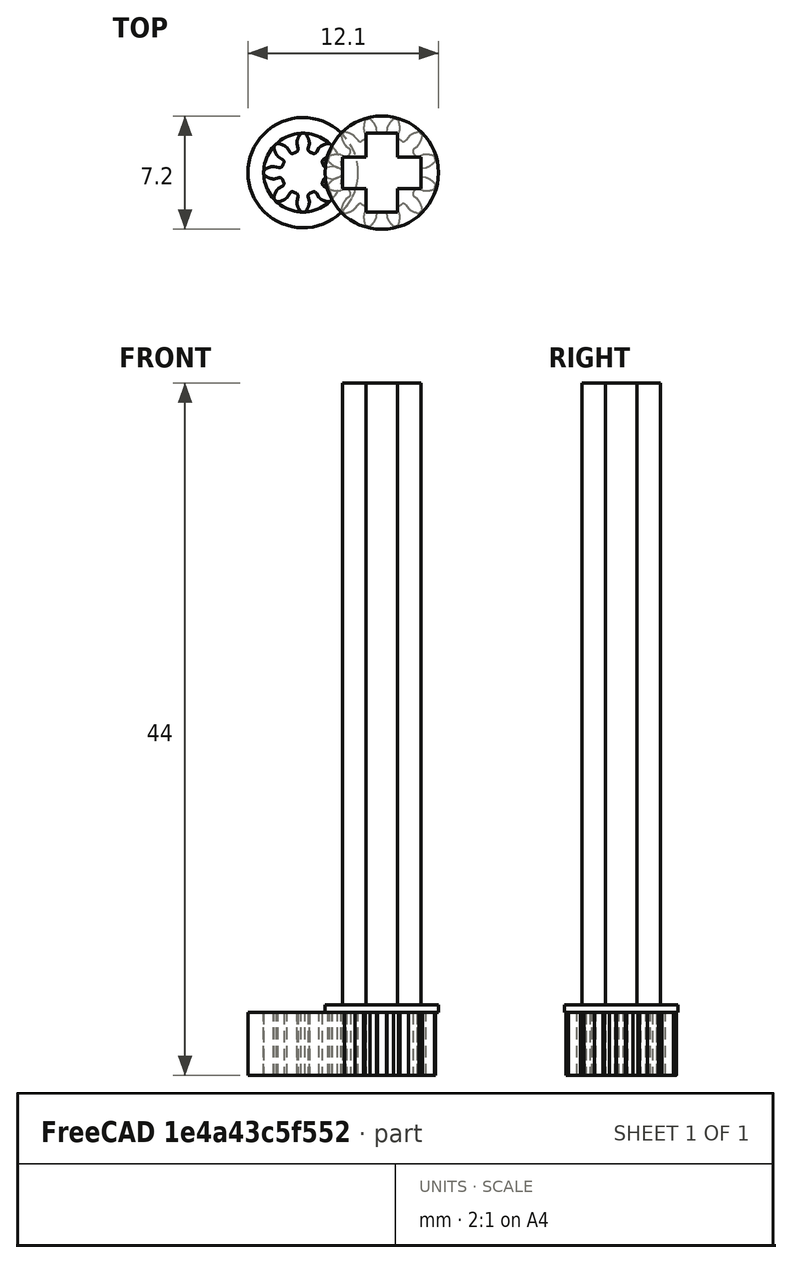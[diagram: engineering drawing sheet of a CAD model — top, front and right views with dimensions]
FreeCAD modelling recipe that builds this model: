
FCSTD DOCUMENT  (FreeCAD 0.20R29177 +426 (Git))
Label: motorGear
License: All rights reserved
LicenseURL: http://en.wikipedia.org/wiki/All_rights_reserved
objects: Part::Cylinder×3, Part::MultiFuse×3, Part::Part2DObjectPython×2, Part::Extrusion×2, Part::Box×2, Mesh::Feature×1
note: 12 computed .brp shape members not serialized (recipe doc carries the construction recipe); baked Part::Feature solids carry a one-line shape summary decoded from their .brp

FEATURE [Part::Cylinder] Cylinder
  Angle = 360
  AttacherType = Attacher::AttachEngine3D
  FirstAngle = 0
  Height = 4
  Radius = 2.5
  SecondAngle = 0
FEATURE [Part::Part2DObjectPython] InvoluteGear  # Draft 2D object (typed FeaturePython)
  ExternalGear = true
  HighPrecision = true
  Modules = 0.5
  NumberOfTeeth = 8
  PressureAngle = 20
FEATURE [Part::Extrusion] Extrude  label="motor"
  Base = -> InvoluteGear
  Dir = (0,0,1)
  DirMode = 2
  FaceMakerClass = Part::FaceMakerBullseye
  LengthFwd = 4
  LengthRev = 0
  Solid = true
  Symmetric = false
FEATURE [Part::Cylinder] Cylinder001
  Angle = 360
  AttacherType = Attacher::AttachEngine3D
  FirstAngle = 0
  Height = 4
  Radius = 3.5
  SecondAngle = 0
FEATURE [Part::Part2DObjectPython] InvoluteGear001  # Draft 2D object (typed FeaturePython)
  ExternalGear = true
  HighPrecision = true
  Modules = 0.5
  NumberOfTeeth = 12
  PressureAngle = 20
FEATURE [Part::Extrusion] Extrude001  label="gear"
  Base = -> InvoluteGear001
  Dir = (0,0,1)
  DirMode = 2
  FaceMakerClass = Part::FaceMakerBullseye
  LengthFwd = 4
  LengthRev = 0
  Placement = pos=(5,0,0) rot=(0,0,1;-0.261799rad)
  Solid = true
  Symmetric = false
FEATURE [Part::Cylinder] Cylinder002
  Angle = 360
  AttacherType = Attacher::AttachEngine3D
  FirstAngle = 0
  Height = 0.5
  Placement = pos=(5,0,4) rot=(0,0,1;0rad)
  Radius = 3.6
  SecondAngle = 0
FEATURE [Part::Box] Box  label="Cube"
  AttacherType = Attacher::AttachEngine3D
  Height = 44
  Length = 2
  Placement = pos=(4,-2.5,0) rot=(0,0,1;0rad)
  Width = 5
FEATURE [Part::Box] Box001  label="Cube001"
  AttacherType = Attacher::AttachEngine3D
  Height = 44
  Length = 5
  Placement = pos=(2.5,-1,0) rot=(0,0,1;0rad)
  Width = 2
FEATURE [Part::MultiFuse] Fusion
  Shapes = -> [Box,Box001]
FEATURE [Part::MultiFuse] Fusion001
  Shapes = -> [Extrude001,Cylinder002]
FEATURE [Part::MultiFuse] Fusion002
  Shapes = -> [Fusion,Fusion001]
FEATURE [Mesh::Feature] Mesh  label="Fusion002 (Meshed)"
